# Revit family: AAL82
name_source: partatom
category: Furniture
revit_build: Autodesk Revit 2016 (Build: 20161004_0715(x64)
units: mm (PartAtom-declared; Revit-internal decimal feet)

## family parameters
Always vertical = Yes
Cut with Voids When Loaded = No
OmniClass Number = 23.40.20.00
OmniClass Title = General Furniture and Specialties
Room Calculation Point = No
Shared = No
Work Plane-Based = No

## types (1)
- AAL82
    Depth = 73cm - 28.74inch
    Description = A spacious and sculpted lounge chair with low back, shaped armrests and round wooden legs. Suitable for a wide range of public and private environments.
    Design = Hee Welling & HAY
    Height = 81cm - 31.89inch
    Legs Left = HAY Matt laquered Oak Vertical
    Legs Right = HAY Matt laquered Oak Horizontal
    Manufacturer = HAY
    Model = AAL 82 Solid wood legs
    Price = Contact HAY or visit hay.dk
    Seat Cushion = HAY Hallingdal - 130
    Seat Height = 36cm - 14.17inch
    Seat cushion optional = Yes
    Shell = HAY Hallingdal - 130
    Strength, durability and safety = EN 16139:2013 L1
    Type Comments = Hard moulded polyurethane foam with armrest. Removable seat cushion in moulded polyurethane foam. Mounted with Velcro upon request.  Also available with moulded plywood legs, swivel base and with high back.
    URL = http://hay.dk
    Upholstery fabric = Available in a large selection of standard fabrics and leathers.
    Upholstery type = Full upholstery
    Variations = Variability of textiles, colours and base finishes.
    Width = 76cm - 29.92inch

## geometry (parser evidence)
native form markers: Sweep x2
no freeform markers — native parametric forms only
